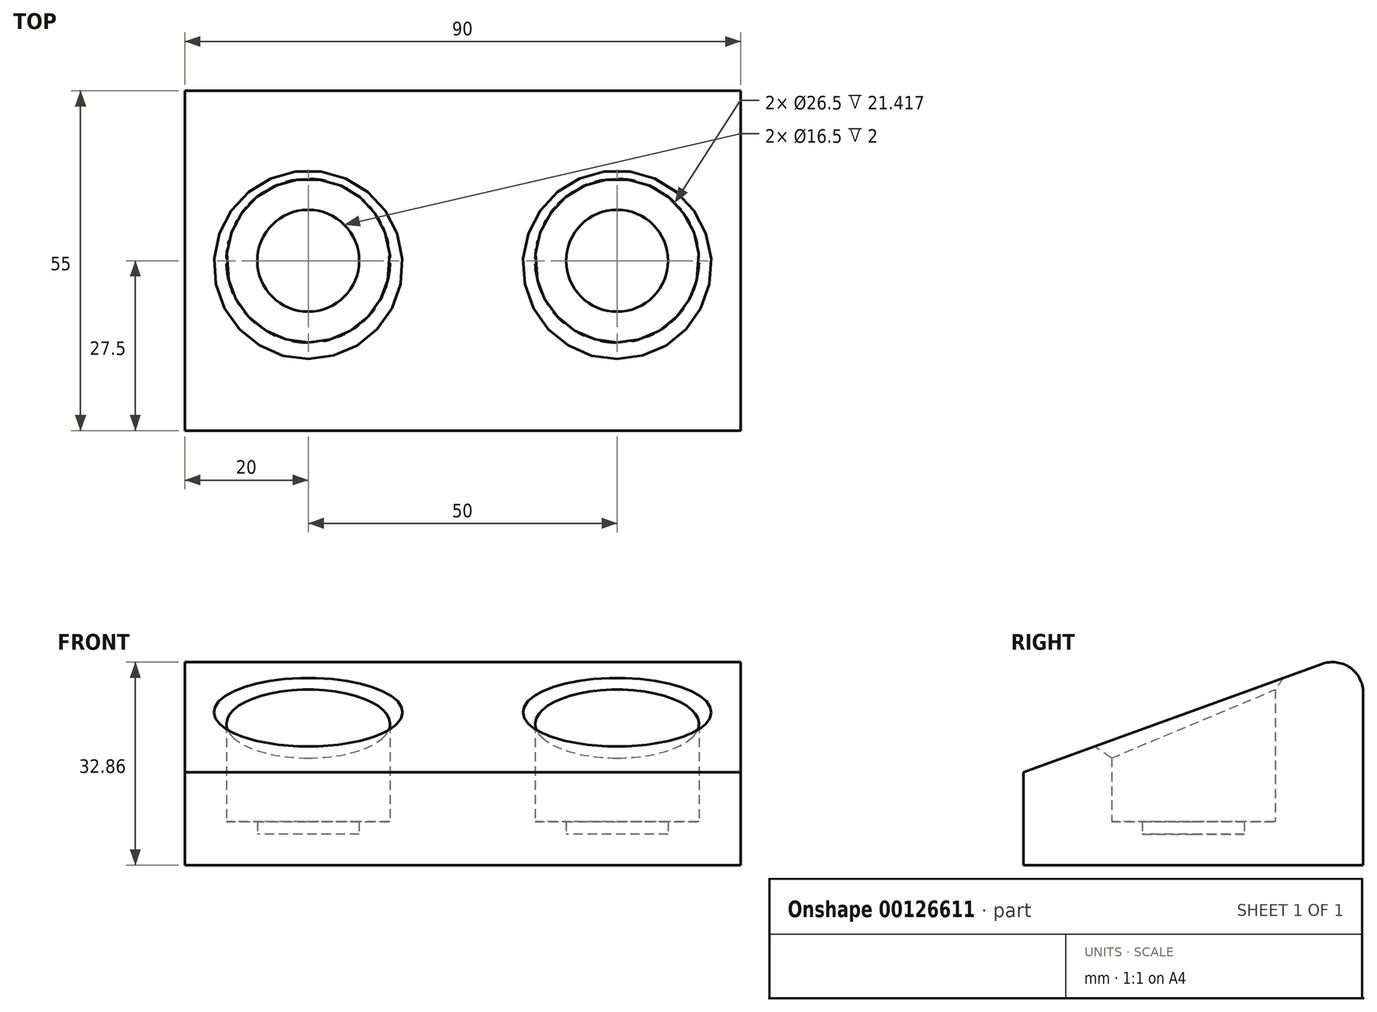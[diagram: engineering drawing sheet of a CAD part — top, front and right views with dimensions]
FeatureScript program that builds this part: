
annotation { "Feature Type Name" : "Feature", "Feature Type Description" : "" }
export const myFeature = defineFeature(function(context is Context, id is Id, definition is map)
    precondition{}
    {
        {
            var Q0;
            Q0=qCreatedBy(makeId("Top.planeOp"),FACE);
            var sketch = newSketch(context, id + "F0", { "sketchPlane" : qUnion([Q0])});
            skLineSegment(sketch, "E0", {"start": v(0, 0) * mm, "end": v(-25, 0) * mm, "construction": true});
            skLineSegment(sketch, "E1", {"start": v(0, 0) * mm, "end": v(25, 0) * mm, "construction": true});
            skLineSegment(sketch, "E2", {"start": v(-25, 0) * mm, "end": v(-10, 0) * mm, "construction": true});
            skLineSegment(sketch, "E3", {"start": v(-25, 0) * mm, "end": v(-25, 24.58) * mm, "construction": true});
            skLineSegment(sketch, "E4", {"start": v(-25, 0) * mm, "end": v(-25, -21.82) * mm, "construction": true});
            skLineSegment(sketch, "E5", {"start": v(-25, 17.5) * mm, "end": v(32.65, 17.5) * mm, "construction": true});
            skLineSegment(sketch, "E6", {"start": v(-25, -17.5) * mm, "end": v(35.4, -17.5) * mm, "construction": true});
            skLineSegment(sketch, "E7", {"start": v(25, 0) * mm, "end": v(25, 19.84) * mm, "construction": true});
            skLineSegment(sketch, "E8", {"start": v(25, 19.84) * mm, "end": v(25.58, -19.79) * mm, "construction": true});
            skLineSegment(sketch, "E9", {"start": v(0, 0) * mm, "end": v(-45, 0) * mm, "construction": true});
            skLineSegment(sketch, "E10", {"start": v(-45, 0) * mm, "end": v(-45, -27.5) * mm, "construction": true});
            skLineSegment(sketch, "E11", {"start": v(-45, 0) * mm, "end": v(-45, 27.5) * mm, "construction": true});
            skLineSegment(sketch, "E12", {"start": v(0, 0) * mm, "end": v(45, 0) * mm, "construction": true});
            skLineSegment(sketch, "E13", {"start": v(45, 0) * mm, "end": v(45, 27.5) * mm, "construction": true});
            skLineSegment(sketch, "E14.bottom", {"start": v(-45, -27.5) * mm, "end": v(45, -27.5) * mm});
            skLineSegment(sketch, "E14.top", {"start": v(-45, 27.5) * mm, "end": v(45, 27.5) * mm});
            skLineSegment(sketch, "E14.left", {"start": v(-45, -27.5) * mm, "end": v(-45, 27.5) * mm});
            skLineSegment(sketch, "E14.right", {"start": v(45, -27.5) * mm, "end": v(45, 27.5) * mm});
            skCircle(sketch, "E15", {"center": v(-25, 0) * mm, "radius": 13.25 * mm});
            skCircle(sketch, "E16", {"center": v(25, 0) * mm, "radius": 13.25 * mm});
            skSolve(sketch);
        }
        {
            var Q0;
            Q0=makeQuery(id+"F0.imprint","IMPRINT",FACE,{"disambiguationData":[TD([[makeQuery(id+"F0.imprint","IMPRINT",EDGE,{"derivedFrom":sQuery(id+"F0.wireOp",EDGE,"vw8SaWjZ-6woT-KxdP-4fa7-yFulkQNvnAhf")}),-1.0]])]});
            var Q1;
            Q1=makeQuery(id+"F0.imprint","IMPRINT",FACE,{"disambiguationData":[TD([[makeQuery(id+"F0.imprint","IMPRINT",EDGE,{"derivedFrom":sQuery(id+"F0.wireOp",EDGE,"E14.bottom")}),1.0]])]});
            extrude(context, id + "F1", {"entities" : qUnion([Q0, Q1]), "depth" : 35 * mm});
        }
        {
            var Q0;
            Q0=makeQuery(id+"F0.imprint","IMPRINT",FACE,{"disambiguationData":[TD([[makeQuery(id+"F0.imprint","IMPRINT",EDGE,{"derivedFrom":sQuery(id+"F0.wireOp",EDGE,"E15")}),1.0]])]});
            var Q1;
            Q1=makeQuery(id+"F0.imprint","IMPRINT",FACE,{"disambiguationData":[TD([[makeQuery(id+"F0.imprint","IMPRINT",EDGE,{"derivedFrom":sQuery(id+"F0.wireOp",EDGE,"E16")}),1.0]])]});
            extrude(context, id + "F2", {"entities" : qUnion([Q0, Q1]), "operationType" : NewBodyOperationType.ADD, "depth" : 5 * mm});
        }
        {
            var Q0;
            Q0=makeQuery(id+"F2.opExtrude","CAP_FACE",FACE,{"disambiguationData":[OSD([sQuery(id+"F0.wireOp",EDGE,"E16")])],"isStart":false});
            var sketch = newSketch(context, id + "F3", { "sketchPlane" : qUnion([Q0])});
            skCircle(sketch, "E17.0.0", {"center": v(-25, 0) * mm, "radius": 13.25 * mm});
            skCircle(sketch, "E18.0", {"center": v(-25, 0) * mm, "radius": 8.25 * mm});
            skCircle(sketch, "E19.0", {"center": v(25, 0) * mm, "radius": 8.25 * mm});
            skSolve(sketch);
        }
        {
            var Q0;
            Q0=makeQuery(id+"F1.opExtrude","SWEPT_FACE",FACE,{"disambiguationData":[OSD([sQuery(id+"F0.wireOp",EDGE,"E14.right")])]});
            var sketch = newSketch(context, id + "F4", { "sketchPlane" : qUnion([Q0])});
            skLineSegment(sketch, "E20", {"start": v(-27.5, 0) * mm, "end": v(-27.5, 15) * mm, "construction": true});
            skLineSegment(sketch, "E21", {"start": v(27.5, 35) * mm, "end": v(-27.5, 15) * mm});
            skSolve(sketch);
        }
        {
            var Q0;
            Q0=qSketchRegion(id+"F4",true);
            var Q1;
            {var subQ0=sQuery(id+"F4.wireOp",EDGE,"E21");Q1=makeQuery(id+"F4.imprint","IMPRINT",FACE,{"disambiguationData":[TD([[makeQuery(id+"F4.imprint","IMPRINT",EDGE,{"derivedFrom":subQ0}),-1.0]])]});}
            extrude(context, id + "F5", {"entities" : qUnion([Q0, Q1]), "operationType" : NewBodyOperationType.REMOVE, "oppositeDirection" : true, "depth" : 90 * mm});
        }
        {
            var Q0;
            {var subQ0=sQuery(id+"F0.wireOp",EDGE,"E14.top");Q0=makeQuery(id+"F5.boolean.opBoolean","MERGE",EDGE,{"derivedFrom":[makeQuery(id+"F1.opExtrude","CAP_EDGE",EDGE,{"disambiguationData":[OSD([subQ0])],"isStart":false}),makeQuery(id+"F5.opExtrude","SWEPT_EDGE",EDGE,{"disambiguationData":[OSD([subQ0,sQuery(id+"F0.wireOp",EDGE,"E14.right"),sQuery(id+"F4.wireOp",EDGE,"E21")])]})]});}
            var Q1;
            Q1=makeQuery(id+"F5.boolean.opBoolean","COPY",EDGE,{"derivedFrom":makeQuery(id+"F5.opExtrude","CAP_EDGE",EDGE,{"disambiguationData":[OSD([sQuery(id+"F4.wireOp",EDGE,"E21")])],"isStart":false})});
            var Q2;
            Q2=makeQuery(id+"F5.boolean.opBoolean","COPY",EDGE,{"derivedFrom":makeQuery(id+"F5.opExtrude","SWEPT_EDGE",EDGE,{"disambiguationData":[OSD([sQuery(id+"F0.wireOp",EDGE,"E14.bottom"),sQuery(id+"F0.wireOp",EDGE,"E14.right"),sQuery(id+"F4.wireOp",EDGE,"E21")])]})});
            var Q3;
            Q3=makeQuery(id+"F5.boolean.opBoolean","COPY",EDGE,{"derivedFrom":makeQuery(id+"F5.opExtrude","CAP_EDGE",EDGE,{"disambiguationData":[OSD([sQuery(id+"F4.wireOp",EDGE,"E21")])],"isStart":true})});
            fillet(context, id + "F6", {"entities" : qUnion([Q0, Q1, Q2, Q3]), "radius" : 5 * mm, "tangentPropagation" : true, "allowEdgeOverflow" : false});
        }
        {
            var Q0;
            Q0=makeQuery(id+"F3.imprint","IMPRINT",FACE,{"disambiguationData":[TD([[makeQuery(id+"F3.imprint","IMPRINT",EDGE,{"derivedFrom":sQuery(id+"F3.wireOp",EDGE,"E17.0.0")}),1.0]])]});
            var Q1;
            Q1=makeQuery(id+"F3.imprint","IMPRINT",FACE,{"disambiguationData":[TD([[makeQuery(id+"F3.imprint","IMPRINT",EDGE,{"derivedFrom":sQuery(id+"F3.wireOp",EDGE,"E19.0")}),-1.0]])]});
            extrude(context, id + "F7", {"entities" : qUnion([Q0, Q1]), "operationType" : NewBodyOperationType.ADD, "depth" : 2 * mm});
        }
        {
            var Q0;
            Q0=makeQuery(id+"F5.boolean.opBoolean","INTERSECT",EDGE,{"derivedFrom":[makeQuery(id+"F1.opExtrude","SWEPT_FACE",FACE,{"disambiguationData":[OSD([sQuery(id+"F0.wireOp",EDGE,"E15")])]}),makeQuery(id+"F5.opExtrude","SWEPT_FACE",FACE,{"disambiguationData":[OSD([sQuery(id+"F4.wireOp",EDGE,"E21")])]})]});
            var Q1;
            Q1=makeQuery(id+"F5.boolean.opBoolean","INTERSECT",EDGE,{"derivedFrom":[makeQuery(id+"F1.opExtrude","SWEPT_FACE",FACE,{"disambiguationData":[OSD([sQuery(id+"F0.wireOp",EDGE,"E16")])]}),makeQuery(id+"F5.opExtrude","SWEPT_FACE",FACE,{"disambiguationData":[OSD([sQuery(id+"F4.wireOp",EDGE,"E21")])]})]});
            chamfer(context, id + "F8", {"entities" : qUnion([Q0, Q1]), "width" : 2 * mm, "tangentPropagation" : true});
        }
    });
